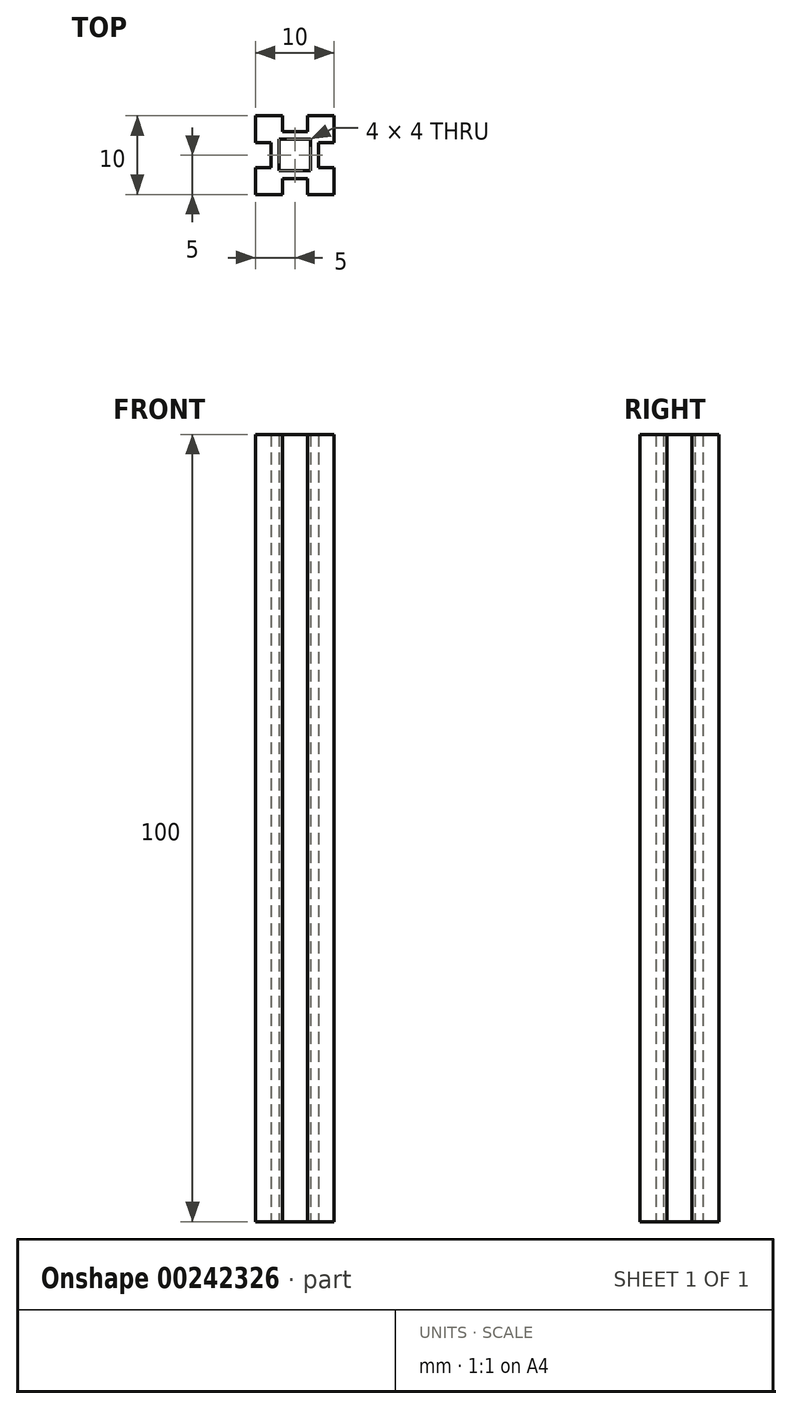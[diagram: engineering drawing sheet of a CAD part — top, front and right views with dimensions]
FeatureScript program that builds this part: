
annotation { "Feature Type Name" : "Feature", "Feature Type Description" : "" }
export const myFeature = defineFeature(function(context is Context, id is Id, definition is map)
    precondition{}
    {
        {
            var Q0;
            Q0=qCreatedBy(makeId("Top.planeOp"),FACE);
            var sketch = newSketch(context, id + "F0", { "sketchPlane" : qUnion([Q0])});
            skLineSegment(sketch, "E0.bottom", {"start": v(5, 5) * mm, "end": v(1.6, 5) * mm});
            skLineSegment(sketch, "E0.right", {"start": v(-5, 5) * mm, "end": v(-5, 1.6) * mm});
            skPoint(sketch, "E0.middle", {"position": v(0, 0) * mm});
            skLineSegment(sketch, "E1.bottom", {"start": v(2, 2) * mm, "end": v(-2, 2) * mm});
            skLineSegment(sketch, "E1.top", {"start": v(2, -2) * mm, "end": v(-2, -2) * mm});
            skLineSegment(sketch, "E1.left", {"start": v(2, 2) * mm, "end": v(2, -2) * mm});
            skLineSegment(sketch, "E1.right", {"start": v(-2, 2) * mm, "end": v(-2, -2) * mm});
            skLineSegment(sketch, "E2", {"start": v(-5, -5) * mm, "end": v(-1.6, -5) * mm});
            skLineSegment(sketch, "E3", {"start": v(5, -5) * mm, "end": v(1.6, -5) * mm});
            skLineSegment(sketch, "E4", {"start": v(-1.6, -5) * mm, "end": v(-1.6, -3) * mm});
            skLineSegment(sketch, "E5", {"start": v(-1.6, -3) * mm, "end": v(1.6, -3) * mm});
            skLineSegment(sketch, "E6", {"start": v(1.6, -3) * mm, "end": v(1.6, -5) * mm});
            skLineSegment(sketch, "E7.MirrorCS", {"start": v(1.6, 3) * mm, "end": v(1.6, 5) * mm});
            skLineSegment(sketch, "E8.MirrorCS", {"start": v(-1.6, 3) * mm, "end": v(1.6, 3) * mm});
            skLineSegment(sketch, "E9.MirrorCS", {"start": v(-1.6, 5) * mm, "end": v(-1.6, 3) * mm});
            skLineSegment(sketch, "E10.trimOffspring", {"start": v(-1.6, 5) * mm, "end": v(-5, 5) * mm});
            skLineSegment(sketch, "E11", {"start": v(5, -5) * mm, "end": v(5, -1.6) * mm});
            skLineSegment(sketch, "E12", {"start": v(5, -1.6) * mm, "end": v(3, -1.6) * mm});
            skLineSegment(sketch, "E13", {"start": v(3, -1.6) * mm, "end": v(3, 1.6) * mm});
            skLineSegment(sketch, "E14", {"start": v(3, 1.6) * mm, "end": v(5, 1.6) * mm});
            skLineSegment(sketch, "E15", {"start": v(5, 1.6) * mm, "end": v(5, 5) * mm});
            skLineSegment(sketch, "E16.MirrorCS", {"start": v(-3, -1.6) * mm, "end": v(-3, 1.6) * mm});
            skLineSegment(sketch, "E17.MirrorCS", {"start": v(-5, -1.6) * mm, "end": v(-3, -1.6) * mm});
            skLineSegment(sketch, "E18.MirrorCS", {"start": v(-3, 1.6) * mm, "end": v(-5, 1.6) * mm});
            skLineSegment(sketch, "E19.trimOffspring", {"start": v(-5, -1.6) * mm, "end": v(-5, -5) * mm});
            skSolve(sketch);
        }
        {
            var Q0;
            Q0 = qSketchRegion(id + "F0", true);
            extrude(context, id + "F1", {"entities" : qUnion([Q0]), "depth" : 100 * mm});
        }
    });
